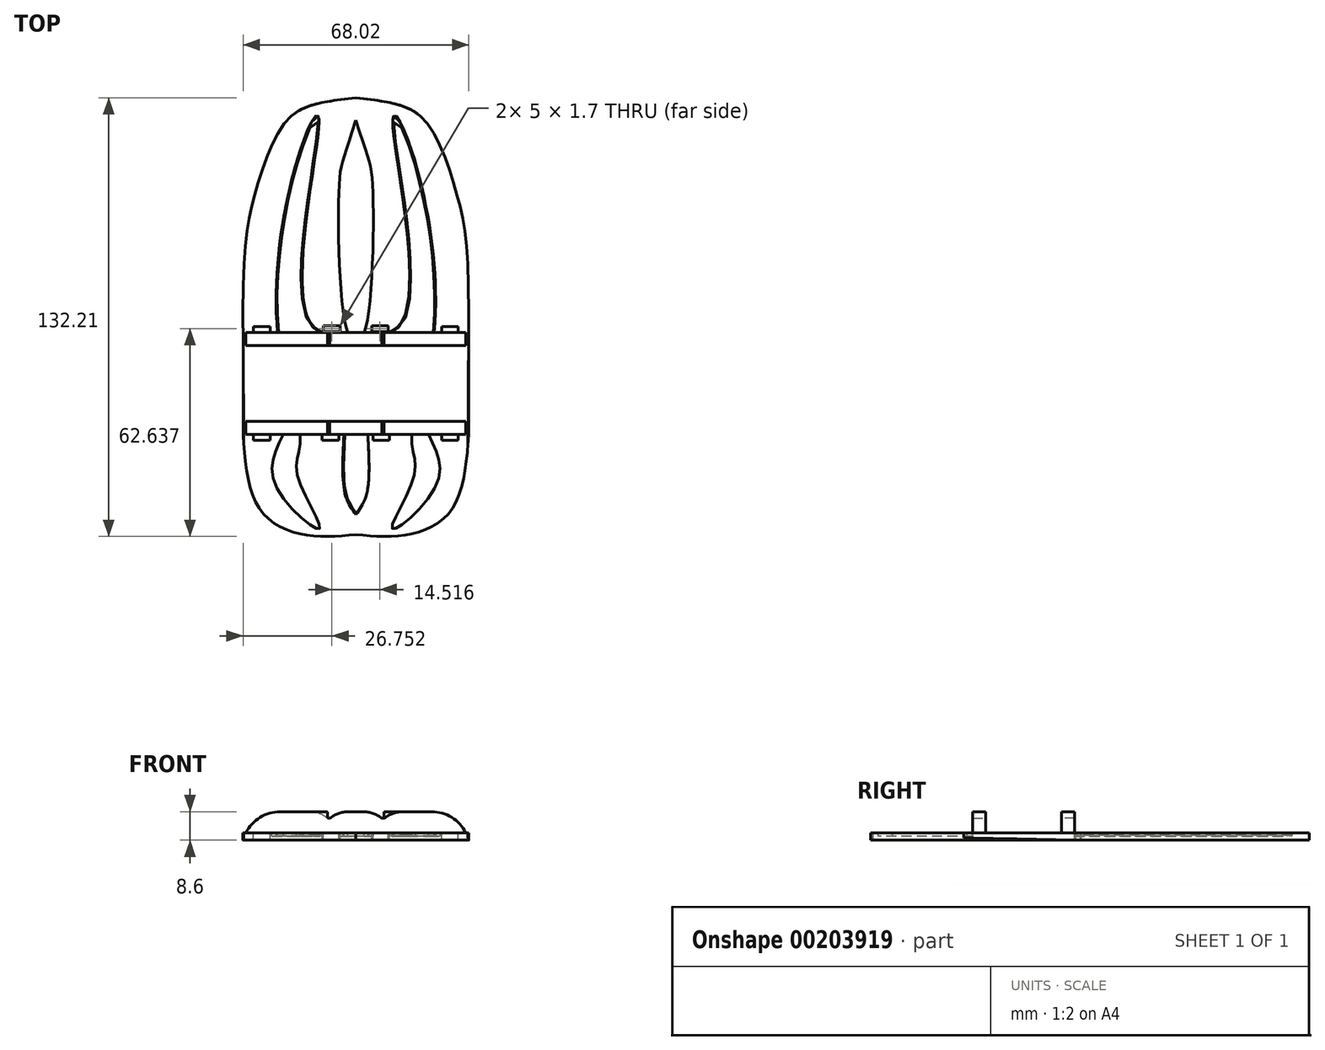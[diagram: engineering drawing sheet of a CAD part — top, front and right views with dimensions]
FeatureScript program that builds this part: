
annotation { "Feature Type Name" : "Feature", "Feature Type Description" : "" }
export const myFeature = defineFeature(function(context is Context, id is Id, definition is map)
    precondition{}
    {
        {
            var Q0;
            Q0=qCreatedBy(makeId("Top.planeOp"),FACE);
            var sketch = newSketch(context, id + "F0", { "sketchPlane" : qUnion([Q0])});
            skLineSegment(sketch, "E0", {"start": v(0, 0) * mm, "end": v(-68, 0) * mm, "construction": true});
            skLineSegment(sketch, "E1", {"start": v(-68, 11.4) * mm, "end": v(0, 11.4) * mm});
            skLineSegment(sketch, "E2.MirrorCS", {"start": v(-68, -11.4) * mm, "end": v(0, -11.4) * mm});
            skLineSegment(sketch, "E3", {"start": v(-68, 11.4) * mm, "end": v(-68, 15.4) * mm});
            skLineSegment(sketch, "E4", {"start": v(-68, 15.4) * mm, "end": v(0, 15.4) * mm});
            skLineSegment(sketch, "E5", {"start": v(0, 15.4) * mm, "end": v(0, 11.4) * mm});
            skLineSegment(sketch, "E6.MirrorCS", {"start": v(-68, -15.4) * mm, "end": v(0, -15.4) * mm});
            skLineSegment(sketch, "E7.MirrorCS", {"start": v(-68, -11.4) * mm, "end": v(-68, -15.4) * mm});
            skLineSegment(sketch, "E8.MirrorCS", {"start": v(0, -15.4) * mm, "end": v(0, -11.4) * mm});
            skLineSegment(sketch, "E9", {"start": v(-34, 15.4) * mm, "end": v(-34, 86.11) * mm, "construction": true});
            skFitSpline(sketch, "E10", {"points": [v(-68, 15.4) * mm, v(-64.11, 58.18) * mm, v(-55.2, 78.83) * mm, v(-34, 86.11) * mm], "startDerivative": vector(-1.19, 195.85) * mm, "endDerivative": vector(120.5, 12.73) * mm});
            skFitSpline(sketch, "E11.MirrorCS", {"points": [v(0, 15.4) * mm, v(-3.89, 58.18) * mm, v(-12.8, 78.83) * mm, v(-34, 86.11) * mm], "startDerivative": vector(1.19, 195.85) * mm, "endDerivative": vector(-120.5, 12.73) * mm});
            skLineSegment(sketch, "E12", {"start": v(-34, -15.4) * mm, "end": v(-34, -45.54) * mm, "construction": true});
            skFitSpline(sketch, "E13", {"points": [v(-68, -15.4) * mm, v(-63, -37.82) * mm, v(-49.83, -45.54) * mm, v(-34, -45.54) * mm], "startDerivative": vector(5.16, -67.49) * mm, "endDerivative": vector(50.73, 4.64) * mm});
            skFitSpline(sketch, "E14.MirrorCS", {"points": [v(0, -15.4) * mm, v(-5, -37.82) * mm, v(-18.17, -45.54) * mm, v(-34, -45.54) * mm], "startDerivative": vector(-5.16, -67.49) * mm, "endDerivative": vector(-50.73, 4.64) * mm});
            skLineSegment(sketch, "E15", {"start": v(-68, 11.4) * mm, "end": v(-68, -11.4) * mm});
            skLineSegment(sketch, "E16", {"start": v(0, -11.4) * mm, "end": v(0, 11.4) * mm});
            skSolve(sketch);
        }
        {
            var Q0;
            Q0=makeQuery(id+"F0.imprint","IMPRINT",FACE,{"disambiguationData":[TD([[makeQuery(id+"F0.imprint","IMPRINT",EDGE,{"derivedFrom":sQuery(id+"F0.wireOp",EDGE,"E4")}),1.0]])]});
            var Q1;
            Q1=makeQuery(id+"F0.imprint","IMPRINT",FACE,{"disambiguationData":[TD([[makeQuery(id+"F0.imprint","IMPRINT",EDGE,{"derivedFrom":sQuery(id+"F0.wireOp",EDGE,"E1")}),-1.0]])]});
            var Q2;
            Q2=makeQuery(id+"F0.imprint","IMPRINT",FACE,{"disambiguationData":[TD([[makeQuery(id+"F0.imprint","IMPRINT",EDGE,{"derivedFrom":sQuery(id+"F0.wireOp",EDGE,"E6.MirrorCS")}),-1.0]])]});
            var Q3;
            Q3=makeQuery(id+"F0.imprint","IMPRINT",FACE,{"disambiguationData":[TD([[makeQuery(id+"F0.imprint","IMPRINT",EDGE,{"derivedFrom":sQuery(id+"F0.wireOp",EDGE,"E2.MirrorCS")}),-1.0]])]});
            var Q4;
            Q4=makeQuery(id+"F0.imprint","IMPRINT",FACE,{"disambiguationData":[TD([[makeQuery(id+"F0.imprint","IMPRINT",EDGE,{"derivedFrom":sQuery(id+"F0.wireOp",EDGE,"E1")}),1.0]])]});
            extrude(context, id + "F1", {"entities" : qUnion([Q0, Q1, Q2, Q3, Q4]), "depth" : 2.2 * mm});
        }
        {
            var Q0;
            Q0=makeQuery(id+"F1.opExtrude","CAP_FACE",FACE,{"disambiguationData":[OSD([sQuery(id+"F0.wireOp",EDGE,"E3"),sQuery(id+"F0.wireOp",EDGE,"E5"),sQuery(id+"F0.wireOp",EDGE,"E7.MirrorCS"),sQuery(id+"F0.wireOp",EDGE,"E8.MirrorCS"),sQuery(id+"F0.wireOp",EDGE,"E10"),sQuery(id+"F0.wireOp",EDGE,"E11.MirrorCS"),sQuery(id+"F0.wireOp",EDGE,"E13"),sQuery(id+"F0.wireOp",EDGE,"E14.MirrorCS"),sQuery(id+"F0.wireOp",EDGE,"E15"),sQuery(id+"F0.wireOp",EDGE,"E16")])],"isStart":false});
            var sketch = newSketch(context, id + "F2", { "sketchPlane" : qUnion([Q0])});
            skFitSpline(sketch, "E17", {"points": [v(-57.61, 15.4) * mm, v(-45.12, 79.72) * mm, v(-44.15, 15.4) * mm], "startDerivative": vector(-18.66, 203.9) * mm, "endDerivative": vector(81.17, -15.6) * mm});
            skLineSegment(sketch, "E18", {"start": v(-34, 86.11) * mm, "end": v(-34, -45.54) * mm, "construction": true});
            skLineSegment(sketch, "E19", {"start": v(0, 15.4) * mm, "end": v(-68, 15.4) * mm, "construction": true});
            skFitSpline(sketch, "E20", {"points": [v(-31.56, 15.4) * mm, v(-28.9, 58.96) * mm, v(-34, 79.42) * mm], "startDerivative": vector(13.25, 28.7) * mm, "endDerivative": vector(-28.42, 91.52) * mm});
            skFitSpline(sketch, "E21.MirrorCS", {"points": [v(-36.44, 15.4) * mm, v(-39.1, 58.96) * mm, v(-34, 79.42) * mm], "startDerivative": vector(-13.25, 28.7) * mm, "endDerivative": vector(28.42, 91.52) * mm});
            skFitSpline(sketch, "E22.MirrorCS", {"points": [v(-10.39, 15.4) * mm, v(-22.88, 79.72) * mm, v(-23.85, 15.4) * mm], "startDerivative": vector(18.66, 203.9) * mm, "endDerivative": vector(-81.17, -15.6) * mm});
            skLineSegment(sketch, "E23", {"start": v(-23.85, 15.4) * mm, "end": v(-10.39, 15.4) * mm});
            skLineSegment(sketch, "E24", {"start": v(-31.56, 15.4) * mm, "end": v(-36.44, 15.4) * mm});
            skLineSegment(sketch, "E25", {"start": v(-44.15, 15.4) * mm, "end": v(-57.61, 15.4) * mm});
            skLineSegment(sketch, "E26", {"start": v(-68, -15.4) * mm, "end": v(0, -15.4) * mm, "construction": true});
            skFitSpline(sketch, "E27", {"points": [v(-55.94, -15.4) * mm, v(-58.3, -30.47) * mm, v(-45, -43.76) * mm, v(-51.59, -27.73) * mm, v(-50.82, -15.4) * mm], "startDerivative": vector(-26.32, -57.17) * mm, "endDerivative": vector(-5.97, 70.05) * mm});
            skFitSpline(sketch, "E28", {"points": [v(-37.6, -15.4) * mm, v(-37.22, -33.42) * mm, v(-34, -39.53) * mm], "startDerivative": vector(-1.8, -33.25) * mm, "endDerivative": vector(9.93, -13.46) * mm});
            skFitSpline(sketch, "E29.MirrorCS", {"points": [v(-30.4, -15.4) * mm, v(-30.78, -33.42) * mm, v(-34, -39.53) * mm], "startDerivative": vector(1.8, -33.25) * mm, "endDerivative": vector(-9.93, -13.46) * mm});
            skFitSpline(sketch, "E30.MirrorCS", {"points": [v(-12.06, -15.4) * mm, v(-9.7, -30.47) * mm, v(-23, -43.76) * mm, v(-16.41, -27.73) * mm, v(-17.18, -15.4) * mm], "startDerivative": vector(26.32, -57.17) * mm, "endDerivative": vector(5.97, 70.05) * mm});
            skLineSegment(sketch, "E31", {"start": v(-12.06, -15.4) * mm, "end": v(-17.18, -15.4) * mm});
            skLineSegment(sketch, "E32", {"start": v(-30.4, -15.4) * mm, "end": v(-37.6, -15.4) * mm});
            skLineSegment(sketch, "E33", {"start": v(-50.82, -15.4) * mm, "end": v(-55.94, -15.4) * mm});
            skLineSegment(sketch, "E34.bottom", {"start": v(-59.87, -15.4) * mm, "end": v(-64.87, -15.4) * mm});
            skLineSegment(sketch, "E34.top", {"start": v(-59.87, -17.1) * mm, "end": v(-64.87, -17.1) * mm});
            skLineSegment(sketch, "E34.left", {"start": v(-59.87, -15.4) * mm, "end": v(-59.87, -17.1) * mm});
            skLineSegment(sketch, "E34.right", {"start": v(-64.87, -15.4) * mm, "end": v(-64.87, -17.1) * mm});
            skLineSegment(sketch, "E35.bottom", {"start": v(-44.15, 15.4) * mm, "end": v(-39.15, 15.4) * mm});
            skLineSegment(sketch, "E36.MirrorCS", {"start": v(-44.15, -17.1) * mm, "end": v(-39.15, -17.1) * mm});
            skLineSegment(sketch, "E37.MirrorCS", {"start": v(-44.15, -15.4) * mm, "end": v(-44.15, -17.1) * mm});
            skLineSegment(sketch, "E38.MirrorCS", {"start": v(-39.15, -15.4) * mm, "end": v(-39.15, -17.1) * mm});
            skLineSegment(sketch, "E39.MirrorCS", {"start": v(-59.87, 15.4) * mm, "end": v(-59.87, 17.1) * mm});
            skLineSegment(sketch, "E40.MirrorCS", {"start": v(-59.87, 17.1) * mm, "end": v(-64.87, 17.1) * mm});
            skLineSegment(sketch, "E41.MirrorCS", {"start": v(-64.87, 15.4) * mm, "end": v(-64.87, 17.1) * mm});
            skLineSegment(sketch, "E42.MirrorCS", {"start": v(-8.13, 15.4) * mm, "end": v(-8.13, 17.1) * mm});
            skLineSegment(sketch, "E43.MirrorCS", {"start": v(-8.13, 17.1) * mm, "end": v(-3.13, 17.1) * mm});
            skLineSegment(sketch, "E44.MirrorCS", {"start": v(-3.13, 15.4) * mm, "end": v(-3.13, 17.1) * mm});
            skLineSegment(sketch, "E45.MirrorCS", {"start": v(-8.13, -15.4) * mm, "end": v(-8.13, -17.1) * mm});
            skLineSegment(sketch, "E46.MirrorCS", {"start": v(-8.13, -17.1) * mm, "end": v(-3.13, -17.1) * mm});
            skLineSegment(sketch, "E47.MirrorCS", {"start": v(-3.13, -15.4) * mm, "end": v(-3.13, -17.1) * mm});
            skLineSegment(sketch, "E48.MirrorCS", {"start": v(-23.85, -15.4) * mm, "end": v(-23.85, -17.1) * mm});
            skLineSegment(sketch, "E49.MirrorCS", {"start": v(-23.85, -17.1) * mm, "end": v(-28.85, -17.1) * mm});
            skLineSegment(sketch, "E50.MirrorCS", {"start": v(-28.85, -15.4) * mm, "end": v(-28.85, -17.1) * mm});
            skLineSegment(sketch, "E51", {"start": v(-39.15, -15.4) * mm, "end": v(-44.15, -15.4) * mm});
            skLineSegment(sketch, "E52", {"start": v(-28.85, -15.4) * mm, "end": v(-23.85, -15.4) * mm});
            skLineSegment(sketch, "E53", {"start": v(-8.13, -15.4) * mm, "end": v(-3.13, -15.4) * mm});
            skLineSegment(sketch, "E54", {"start": v(-8.13, 15.4) * mm, "end": v(-3.13, 15.4) * mm});
            skLineSegment(sketch, "E55", {"start": v(-23.85, 15.4) * mm, "end": v(-28.85, 15.4) * mm});
            skLineSegment(sketch, "E56", {"start": v(-39.15, 15.4) * mm, "end": v(-44.15, 15.4) * mm});
            skLineSegment(sketch, "E57", {"start": v(-59.87, 15.4) * mm, "end": v(-64.87, 15.4) * mm});
            skLineSegment(sketch, "E58", {"start": v(-43.76, 15.4) * mm, "end": v(-43.76, 15.69) * mm, "construction": true});
            skLineSegment(sketch, "E59", {"start": v(-38.76, 15.69) * mm, "end": v(-38.76, 15.4) * mm, "construction": true});
            skLineSegment(sketch, "E60", {"start": v(-38.76, 15.69) * mm, "end": v(-38.76, 17.39) * mm});
            skLineSegment(sketch, "E61", {"start": v(-38.76, 17.39) * mm, "end": v(-43.76, 17.39) * mm});
            skLineSegment(sketch, "E62", {"start": v(-43.76, 17.39) * mm, "end": v(-43.76, 15.69) * mm});
            skLineSegment(sketch, "E63.MirrorCS", {"start": v(-29.24, 17.39) * mm, "end": v(-24.24, 17.39) * mm});
            skLineSegment(sketch, "E64.MirrorCS", {"start": v(-24.24, 17.39) * mm, "end": v(-24.24, 15.69) * mm});
            skLineSegment(sketch, "E65.MirrorCS", {"start": v(-29.24, 15.69) * mm, "end": v(-29.24, 17.39) * mm});
            skLineSegment(sketch, "E66", {"start": v(-38.76, 15.69) * mm, "end": v(-43.76, 15.69) * mm});
            skLineSegment(sketch, "E67", {"start": v(-29.24, 15.69) * mm, "end": v(-24.24, 15.69) * mm});
            skSolve(sketch);
        }
        {
            var Q0;
            Q0 = qSketchRegion(id + "F2", true);
            extrude(context, id + "F3", {"entities" : qUnion([Q0]), "operationType" : NewBodyOperationType.REMOVE, "depth" : 0.5 * mm});
        }
        {
            var Q0;
            Q0=makeQuery(id+"F0.imprint","IMPRINT",FACE,{"disambiguationData":[TD([[makeQuery(id+"F0.imprint","IMPRINT",EDGE,{"derivedFrom":sQuery(id+"F0.wireOp",EDGE,"E2.MirrorCS")}),-1.0]])]});
            var Q1;
            Q1=makeQuery(id+"F0.imprint","IMPRINT",FACE,{"disambiguationData":[TD([[makeQuery(id+"F0.imprint","IMPRINT",EDGE,{"derivedFrom":sQuery(id+"F0.wireOp",EDGE,"E1")}),1.0]])]});
            extrude(context, id + "F4", {"entities" : qUnion([Q0, Q1]), "operationType" : NewBodyOperationType.ADD, "depth" : 8.6 * mm});
        }
        {
            var Q0;
            Q0=makeQuery(id+"F4.opExtrude","CAP_EDGE",EDGE,{"disambiguationData":[OSD([sQuery(id+"F0.wireOp",EDGE,"E7.MirrorCS")])],"isStart":false});
            var Q1;
            Q1=makeQuery(id+"F4.opExtrude","CAP_EDGE",EDGE,{"disambiguationData":[OSD([sQuery(id+"F0.wireOp",EDGE,"E3")])],"isStart":false});
            var Q2;
            Q2=makeQuery(id+"F4.opExtrude","CAP_EDGE",EDGE,{"disambiguationData":[OSD([sQuery(id+"F0.wireOp",EDGE,"E5")])],"isStart":false});
            var Q3;
            Q3=makeQuery(id+"F4.opExtrude","CAP_EDGE",EDGE,{"disambiguationData":[OSD([sQuery(id+"F0.wireOp",EDGE,"E8.MirrorCS")])],"isStart":false});
            fillet(context, id + "F5", {"entities" : qUnion([Q0, Q1, Q2, Q3]), "radius" : 11.6 * mm, "tangentPropagation" : true, "allowEdgeOverflow" : false});
        }
        {
            var Q0;
            Q0=makeQuery(id+"F2.imprint","IMPRINT",FACE,{"disambiguationData":[TD([[makeQuery(id+"F2.imprint","IMPRINT",EDGE,{"derivedFrom":sQuery(id+"F2.wireOp",EDGE,"E20")}),1.0]])]});
            var Q1;
            Q1=makeQuery(id+"F2.imprint","IMPRINT",FACE,{"disambiguationData":[TD([[makeQuery(id+"F2.imprint","IMPRINT",EDGE,{"derivedFrom":sQuery(id+"F2.wireOp",EDGE,"E27")}),1.0]])]});
            var Q2;
            Q2=makeQuery(id+"F2.imprint","IMPRINT",FACE,{"disambiguationData":[TD([[makeQuery(id+"F2.imprint","IMPRINT",EDGE,{"derivedFrom":sQuery(id+"F2.wireOp",EDGE,"E30.MirrorCS")}),-1.0]])]});
            var Q3;
            Q3=makeQuery(id+"F2.imprint","IMPRINT",FACE,{"disambiguationData":[TD([[makeQuery(id+"F2.imprint","IMPRINT",EDGE,{"derivedFrom":sQuery(id+"F2.wireOp",EDGE,"E28")}),1.0]])]});
            var Q4;
            Q4=makeQuery(id+"F2.imprint","IMPRINT",FACE,{"disambiguationData":[TD([[makeQuery(id+"F2.imprint","IMPRINT",EDGE,{"derivedFrom":sQuery(id+"F2.wireOp",EDGE,"E17")}),-1.0]])]});
            var Q5;
            Q5=makeQuery(id+"F2.imprint","IMPRINT",FACE,{"disambiguationData":[TD([[makeQuery(id+"F2.imprint","IMPRINT",EDGE,{"derivedFrom":sQuery(id+"F2.wireOp",EDGE,"E22.MirrorCS")}),1.0]])]});
            extrude(context, id + "F6", {"entities" : qUnion([Q0, Q1, Q2, Q3, Q4, Q5]), "operationType" : NewBodyOperationType.REMOVE, "oppositeDirection" : true, "depth" : 1 * mm});
        }
        {
            var Q0;
            Q0=makeQuery(id+"F6.boolean.opBoolean","COPY",EDGE,{"derivedFrom":makeQuery(id+"F6.opExtrude","CAP_EDGE",EDGE,{"disambiguationData":[OSD([sQuery(id+"F2.wireOp",EDGE,"E21.MirrorCS")])],"isStart":true})});
            var Q1;
            Q1=makeQuery(id+"F6.boolean.opBoolean","COPY",EDGE,{"derivedFrom":makeQuery(id+"F6.opExtrude","CAP_EDGE",EDGE,{"disambiguationData":[OSD([sQuery(id+"F2.wireOp",EDGE,"E20")])],"isStart":true})});
            var Q2;
            Q2=makeQuery(id+"F6.boolean.opBoolean","COPY",EDGE,{"derivedFrom":makeQuery(id+"F6.opExtrude","CAP_EDGE",EDGE,{"disambiguationData":[OSD([sQuery(id+"F2.wireOp",EDGE,"E22.MirrorCS")])],"isStart":false})});
            var Q3;
            Q3=makeQuery(id+"F6.boolean.opBoolean","COPY",EDGE,{"derivedFrom":makeQuery(id+"F6.opExtrude","CAP_EDGE",EDGE,{"disambiguationData":[OSD([sQuery(id+"F2.wireOp",EDGE,"E30.MirrorCS")])],"isStart":true})});
            var Q4;
            Q4=makeQuery(id+"F6.boolean.opBoolean","COPY",EDGE,{"derivedFrom":makeQuery(id+"F6.opExtrude","CAP_EDGE",EDGE,{"disambiguationData":[OSD([sQuery(id+"F2.wireOp",EDGE,"E29.MirrorCS")])],"isStart":true})});
            var Q5;
            Q5=makeQuery(id+"F6.boolean.opBoolean","COPY",EDGE,{"derivedFrom":makeQuery(id+"F6.opExtrude","CAP_EDGE",EDGE,{"disambiguationData":[OSD([sQuery(id+"F2.wireOp",EDGE,"E28")])],"isStart":false})});
            var Q6;
            Q6=makeQuery(id+"F6.boolean.opBoolean","COPY",EDGE,{"derivedFrom":makeQuery(id+"F6.opExtrude","CAP_EDGE",EDGE,{"disambiguationData":[OSD([sQuery(id+"F2.wireOp",EDGE,"E27")])],"isStart":true})});
            var Q7;
            Q7=makeQuery(id+"F6.boolean.opBoolean","COPY",EDGE,{"derivedFrom":makeQuery(id+"F6.opExtrude","CAP_EDGE",EDGE,{"disambiguationData":[OSD([sQuery(id+"F2.wireOp",EDGE,"E17")])],"isStart":false})});
            fillet(context, id + "F7", {"entities" : qUnion([Q0, Q1, Q2, Q3, Q4, Q5, Q6, Q7]), "radius" : 0.3 * mm, "tangentPropagation" : true, "allowEdgeOverflow" : false});
        }
        {
            var Q0;
            Q0=makeQuery(id+"F2.imprint","IMPRINT",FACE,{"disambiguationData":[TD([[makeQuery(id+"F2.imprint","IMPRINT",EDGE,{"derivedFrom":sQuery(id+"F2.wireOp",EDGE,"E34.top")}),-1.0]])]});
            var Q1;
            Q1=makeQuery(id+"F2.imprint","IMPRINT",FACE,{"disambiguationData":[TD([[makeQuery(id+"F2.imprint","IMPRINT",EDGE,{"derivedFrom":sQuery(id+"F2.wireOp",EDGE,"E36.MirrorCS")}),1.0]])]});
            var Q2;
            Q2=makeQuery(id+"F2.imprint","IMPRINT",FACE,{"disambiguationData":[TD([[makeQuery(id+"F2.imprint","IMPRINT",EDGE,{"derivedFrom":sQuery(id+"F2.wireOp",EDGE,"E48.MirrorCS")}),-1.0]])]});
            var Q3;
            Q3=makeQuery(id+"F2.imprint","IMPRINT",FACE,{"disambiguationData":[TD([[makeQuery(id+"F2.imprint","IMPRINT",EDGE,{"derivedFrom":sQuery(id+"F2.wireOp",EDGE,"E45.MirrorCS")}),1.0]])]});
            var Q4;
            Q4=makeQuery(id+"F2.imprint","IMPRINT",FACE,{"disambiguationData":[TD([[makeQuery(id+"F2.imprint","IMPRINT",EDGE,{"derivedFrom":sQuery(id+"F2.wireOp",EDGE,"E42.MirrorCS")}),-1.0]])]});
            var Q5;
            Q5=makeQuery(id+"F2.imprint","IMPRINT",FACE,{"disambiguationData":[TD([[makeQuery(id+"F2.imprint","IMPRINT",EDGE,{"derivedFrom":sQuery(id+"F2.wireOp",EDGE,"E39.MirrorCS")}),1.0]])]});
            var Q6;
            Q6=makeQuery(id+"F2.imprint","IMPRINT",FACE,{"disambiguationData":[TD([[makeQuery(id+"F2.imprint","IMPRINT",EDGE,{"derivedFrom":sQuery(id+"F2.wireOp",EDGE,"E60")}),1.0]])]});
            var Q7;
            Q7=makeQuery(id+"F2.imprint","IMPRINT",FACE,{"disambiguationData":[TD([[makeQuery(id+"F2.imprint","IMPRINT",EDGE,{"derivedFrom":sQuery(id+"F2.wireOp",EDGE,"E63.MirrorCS")}),-1.0]])]});
            extrude(context, id + "F8", {"entities" : qUnion([Q0, Q1, Q2, Q3, Q4, Q5, Q6, Q7]), "operationType" : NewBodyOperationType.REMOVE, "endBound" : BoundingType.THROUGH_ALL, "oppositeDirection" : true, "depth" : 25 * mm});
        }
        {
            var Q0;
            Q0=makeQuery(id+"F4.opExtrude","CAP_FACE",FACE,{"disambiguationData":[OSD([sQuery(id+"F0.wireOp",EDGE,"E1"),sQuery(id+"F0.wireOp",EDGE,"E3"),sQuery(id+"F0.wireOp",EDGE,"E4"),sQuery(id+"F0.wireOp",EDGE,"E5")])],"isStart":false});
            var sketch = newSketch(context, id + "F9", { "sketchPlane" : qUnion([Q0])});
            skLineSegment(sketch, "E68", {"start": v(-42.5, 15.4) * mm, "end": v(-42.5, 11.4) * mm});
            skLineSegment(sketch, "E69", {"start": v(-42.5, 11.4) * mm, "end": v(-41.87, 11.4) * mm});
            skLineSegment(sketch, "E70", {"start": v(-41.87, 11.4) * mm, "end": v(-41.87, 15.4) * mm});
            skLineSegment(sketch, "E71", {"start": v(-41.87, 15.4) * mm, "end": v(-42.5, 15.4) * mm});
            skLineSegment(sketch, "E72.MirrorCS", {"start": v(-26.13, 11.4) * mm, "end": v(-26.13, 15.4) * mm});
            skLineSegment(sketch, "E73.MirrorCS", {"start": v(-25.5, 15.4) * mm, "end": v(-25.5, 11.4) * mm});
            skLineSegment(sketch, "E74.MirrorCS", {"start": v(-25.5, 11.4) * mm, "end": v(-26.13, 11.4) * mm});
            skLineSegment(sketch, "E75.MirrorCS", {"start": v(-26.13, 15.4) * mm, "end": v(-25.5, 15.4) * mm});
            skLineSegment(sketch, "E76.MirrorCS", {"start": v(-41.87, -11.4) * mm, "end": v(-41.87, -15.4) * mm});
            skLineSegment(sketch, "E77.MirrorCS", {"start": v(-42.5, -15.4) * mm, "end": v(-42.5, -11.4) * mm});
            skLineSegment(sketch, "E78.MirrorCS", {"start": v(-41.87, -15.4) * mm, "end": v(-42.5, -15.4) * mm});
            skLineSegment(sketch, "E79.MirrorCS", {"start": v(-42.5, -11.4) * mm, "end": v(-41.87, -11.4) * mm});
            skLineSegment(sketch, "E80.MirrorCS", {"start": v(-26.13, -15.4) * mm, "end": v(-25.5, -15.4) * mm});
            skLineSegment(sketch, "E81.MirrorCS", {"start": v(-26.13, -11.4) * mm, "end": v(-26.13, -15.4) * mm});
            skLineSegment(sketch, "E82.MirrorCS", {"start": v(-25.5, -15.4) * mm, "end": v(-25.5, -11.4) * mm});
            skLineSegment(sketch, "E83.MirrorCS", {"start": v(-25.5, -11.4) * mm, "end": v(-26.13, -11.4) * mm});
            skSolve(sketch);
        }
        {
            var Q0;
            Q0 = qSketchRegion(id + "F9", true);
            extrude(context, id + "F10", {"entities" : qUnion([Q0]), "operationType" : NewBodyOperationType.REMOVE, "oppositeDirection" : true, "depth" : 2 * mm});
        }
        {
            var Q0;
            Q0=makeQuery(id+"F10.boolean.opBoolean","COPY",EDGE,{"derivedFrom":makeQuery(id+"F10.opExtrude","CAP_EDGE",EDGE,{"disambiguationData":[OSD([sQuery(id+"F9.wireOp",EDGE,"E68")])],"isStart":true})});
            var Q1;
            Q1=makeQuery(id+"F10.boolean.opBoolean","COPY",EDGE,{"derivedFrom":makeQuery(id+"F10.opExtrude","CAP_EDGE",EDGE,{"disambiguationData":[OSD([sQuery(id+"F9.wireOp",EDGE,"E70")])],"isStart":true})});
            var Q2;
            Q2=makeQuery(id+"F10.boolean.opBoolean","COPY",EDGE,{"derivedFrom":makeQuery(id+"F10.opExtrude","CAP_EDGE",EDGE,{"disambiguationData":[OSD([sQuery(id+"F9.wireOp",EDGE,"E72.MirrorCS")])],"isStart":true})});
            var Q3;
            Q3=makeQuery(id+"F10.boolean.opBoolean","COPY",EDGE,{"derivedFrom":makeQuery(id+"F10.opExtrude","CAP_EDGE",EDGE,{"disambiguationData":[OSD([sQuery(id+"F9.wireOp",EDGE,"E73.MirrorCS")])],"isStart":true})});
            var Q4;
            Q4=makeQuery(id+"F10.boolean.opBoolean","COPY",EDGE,{"derivedFrom":makeQuery(id+"F10.opExtrude","CAP_EDGE",EDGE,{"disambiguationData":[OSD([sQuery(id+"F9.wireOp",EDGE,"E76.MirrorCS")])],"isStart":true})});
            var Q5;
            Q5=makeQuery(id+"F10.boolean.opBoolean","COPY",EDGE,{"derivedFrom":makeQuery(id+"F10.opExtrude","CAP_EDGE",EDGE,{"disambiguationData":[OSD([sQuery(id+"F9.wireOp",EDGE,"E77.MirrorCS")])],"isStart":true})});
            var Q6;
            Q6=makeQuery(id+"F10.boolean.opBoolean","COPY",EDGE,{"derivedFrom":makeQuery(id+"F10.opExtrude","CAP_EDGE",EDGE,{"disambiguationData":[OSD([sQuery(id+"F9.wireOp",EDGE,"E81.MirrorCS")])],"isStart":true})});
            var Q7;
            Q7=makeQuery(id+"F10.boolean.opBoolean","COPY",EDGE,{"derivedFrom":makeQuery(id+"F10.opExtrude","CAP_EDGE",EDGE,{"disambiguationData":[OSD([sQuery(id+"F9.wireOp",EDGE,"E82.MirrorCS")])],"isStart":true})});
            fillet(context, id + "F11", {"entities" : qUnion([Q0, Q1, Q2, Q3, Q4, Q5, Q6, Q7]), "radius" : 9.17 * mm, "tangentPropagation" : true, "allowEdgeOverflow" : false});
        }
    });
